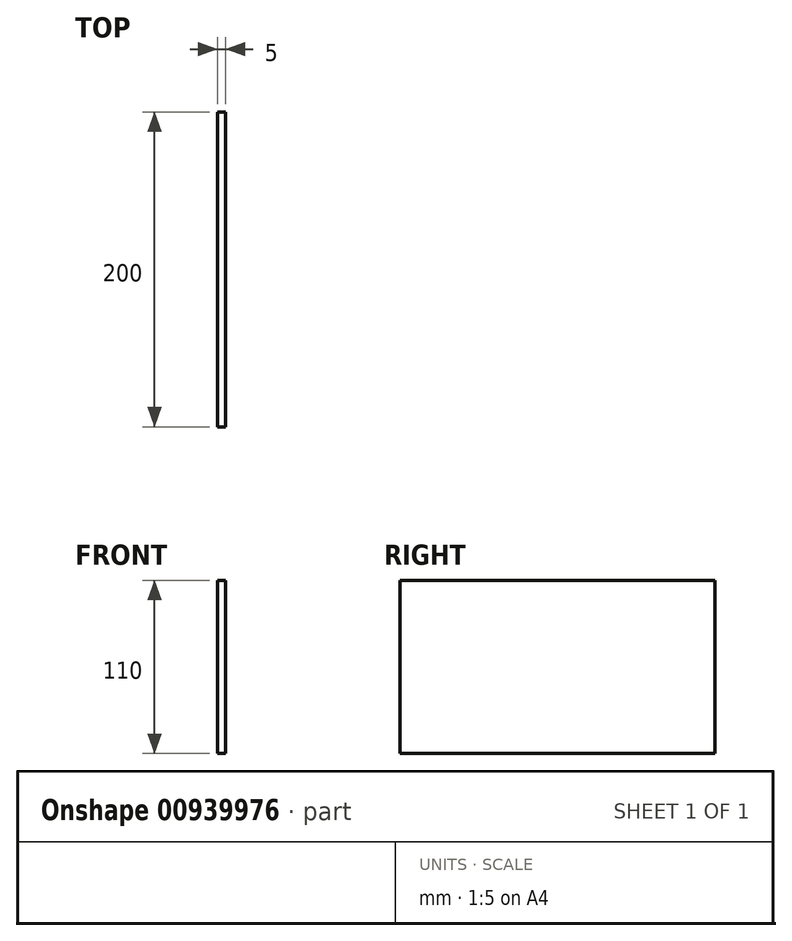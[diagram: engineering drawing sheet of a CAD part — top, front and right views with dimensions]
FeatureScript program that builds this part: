
annotation { "Feature Type Name" : "Feature", "Feature Type Description" : "" }
export const myFeature = defineFeature(function(context is Context, id is Id, definition is map)
    precondition{}
    {
        {
            var Q0;
            Q0=qCreatedBy(makeId("Right.planeOp"),FACE);
            var sketch = newSketch(context, id + "F0", { "sketchPlane" : qUnion([Q0])});
            skLineSegment(sketch, "E0.bottom", {"start": v(0, 0) * mm, "end": v(200, 0) * mm});
            skLineSegment(sketch, "E0.top", {"start": v(0, 110) * mm, "end": v(200, 110) * mm});
            skLineSegment(sketch, "E0.left", {"start": v(0, 0) * mm, "end": v(0, 110) * mm});
            skLineSegment(sketch, "E0.right", {"start": v(200, 0) * mm, "end": v(200, 110) * mm});
            skSolve(sketch);
        }
        {
            var Q0;
            Q0=makeQuery(id+"F0.imprint","IMPRINT",FACE,{"disambiguationData":[TD([[makeQuery(id+"F0.imprint","IMPRINT",EDGE,{"derivedFrom":sQuery(id+"F0.wireOp",EDGE,"E0.bottom")}),1.0]])]});
            extrude(context, id + "F1", {"entities" : qUnion([Q0]), "depth" : 5 * mm, "offsetDistance" : 25 * mm});
        }
    });
